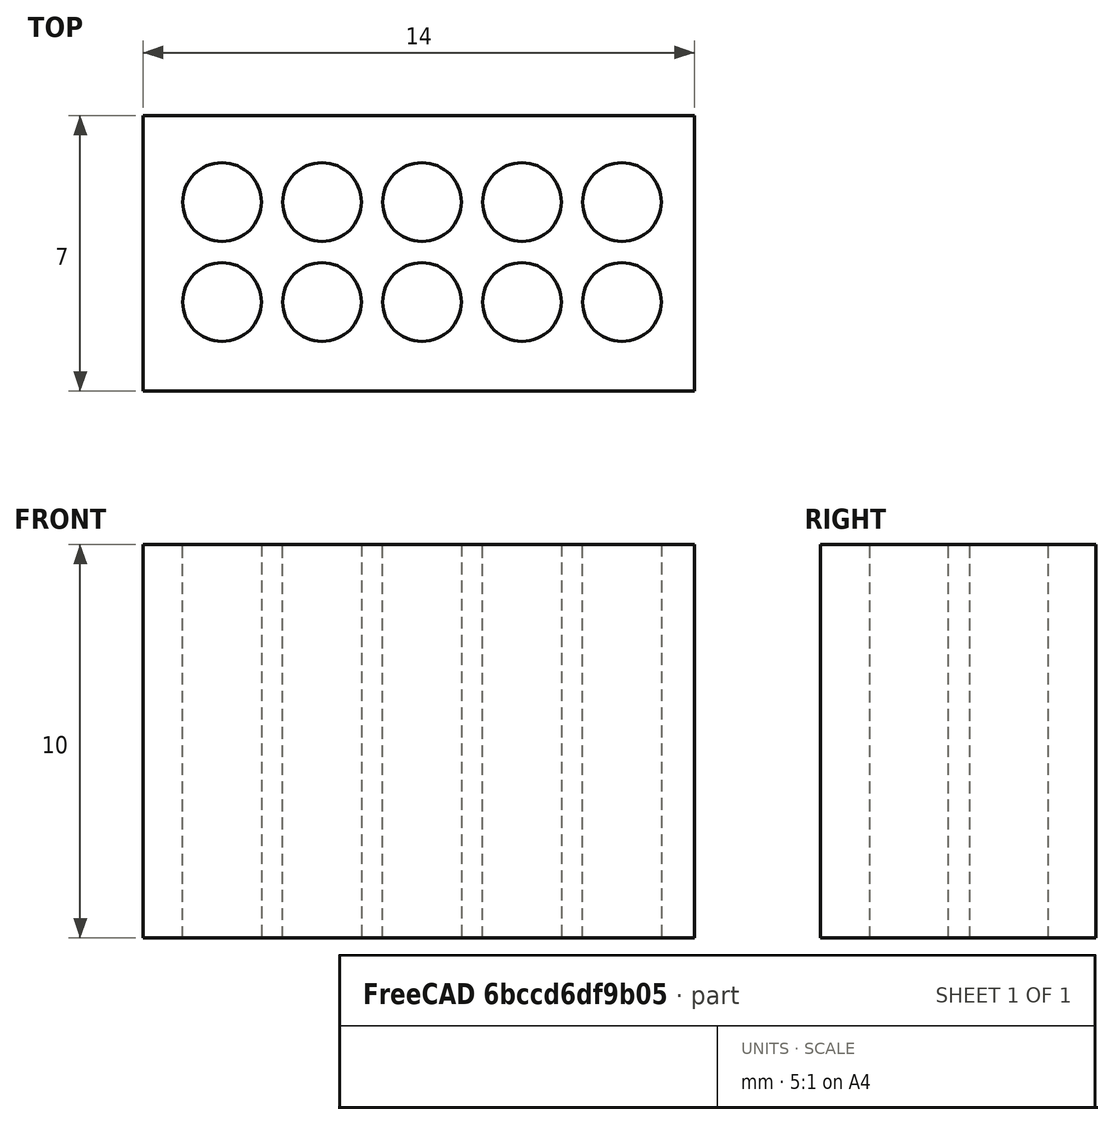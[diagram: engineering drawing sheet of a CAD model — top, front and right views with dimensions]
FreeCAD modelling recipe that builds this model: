
FCSTD DOCUMENT  (FreeCAD 0.16R6712 (Git))
Label: PogoProgrammer01
License: All rights reserved
LicenseURL: http://en.wikipedia.org/wiki/All_rights_reserved
objects: Part::Box×1, Sketcher::SketchObject×1, PartDesign::Pocket×1
note: 4 computed .brp shape members not serialized (recipe doc carries the construction recipe); baked Part::Feature solids carry a one-line shape summary decoded from their .brp

FEATURE [Part::Box] Box  label="Cube"
  Height = 10
  Length = 14
  Width = 7
FEATURE [Sketcher::SketchObject] Sketch
  Placement = pos=(0,0,10) rot=(0,0,1;0rad)
  Support = -> Box [Face6]
  sketch-geometry (10):
    g0: Circle CenterX=2 CenterY=2.26 CenterZ=0 NormalX=0 NormalY=0 NormalZ=1 Radius=1
    g1: Circle CenterX=4.54 CenterY=2.26 CenterZ=0 NormalX=0 NormalY=0 NormalZ=1 Radius=1
    g2: Circle CenterX=7.08 CenterY=2.26 CenterZ=0 NormalX=0 NormalY=0 NormalZ=1 Radius=1
    g3: Circle CenterX=9.62 CenterY=2.26 CenterZ=0 NormalX=0 NormalY=0 NormalZ=1 Radius=1
    g4: Circle CenterX=12.16 CenterY=2.26 CenterZ=0 NormalX=0 NormalY=0 NormalZ=1 Radius=1
    g5: Circle CenterX=2 CenterY=4.8 CenterZ=0 NormalX=0 NormalY=0 NormalZ=1 Radius=1
    g6: Circle CenterX=4.54 CenterY=4.8 CenterZ=0 NormalX=0 NormalY=0 NormalZ=1 Radius=1
    g7: Circle CenterX=7.08 CenterY=4.8 CenterZ=0 NormalX=0 NormalY=0 NormalZ=1 Radius=1
    g8: Circle CenterX=9.62 CenterY=4.8 CenterZ=0 NormalX=0 NormalY=0 NormalZ=1 Radius=1
    g9: Circle CenterX=12.16 CenterY=4.8 CenterZ=0 NormalX=0 NormalY=0 NormalZ=1 Radius=1
  constraints (22):
    c: Radius(g0) = 1
    c: DistanceX(g1,g2) = 2.54
    c: DistanceX(g2,g3) = 2.54
    c: DistanceX(g3,g4) = 2.54
    c: DistanceX(g0,g1) = 2.54
    c: Equal(g0,g5) = 1
    c: DistanceX(g6,g7) = 2.54
    c: DistanceX(g7,g8) = 2.54
    c: DistanceX(g8,g9) = 2.54
    c: DistanceX(g5,g6) = 2.54
    c: DistanceY(g0,g5) = 2.54
    c: DistanceY(g1,g6) = 2.54
    c: DistanceY(g2,g7) = 2.54
    c: DistanceY(g3,g8) = 2.54
    c: DistanceY(g4,g9) = 2.54
    c: DistanceX(g-1,g0) = 2
    c: DistanceX(g-2,g5) = 2
    c: DistanceY(g-1,g4) = 2.26
    c: DistanceY(g-1,g3) = 2.26
    c: DistanceY(g-1,g2) = 2.26
    c: DistanceY(g-1,g1) = 2.26
    c: DistanceY(g-1,g0) = 2.26
FEATURE [PartDesign::Pocket] Pocket
  Length = 10
  Sketch = -> Sketch
  Type = 0
